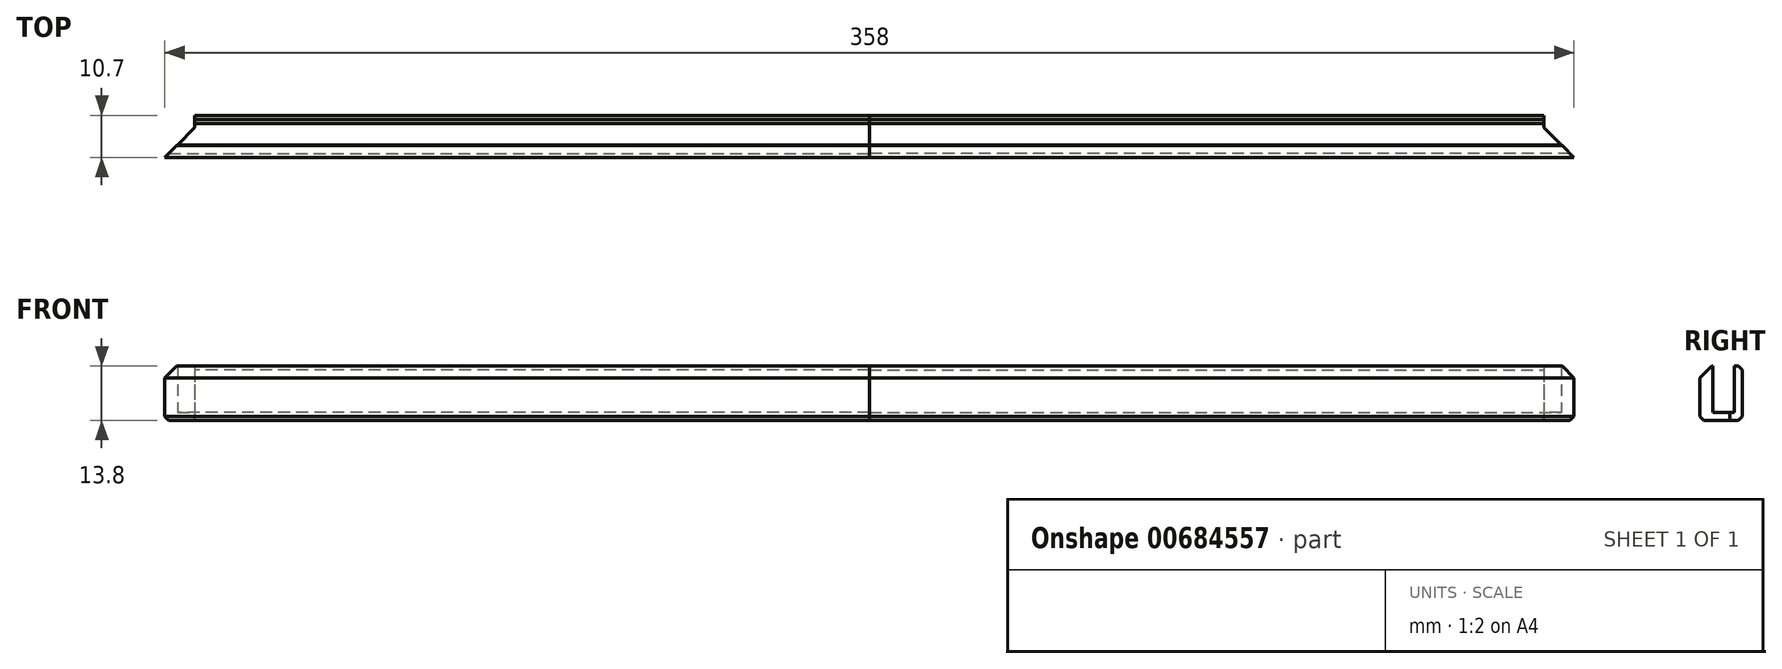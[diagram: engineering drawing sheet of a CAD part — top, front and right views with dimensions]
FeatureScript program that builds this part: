
annotation { "Feature Type Name" : "Feature", "Feature Type Description" : "" }
export const myFeature = defineFeature(function(context is Context, id is Id, definition is map)
    precondition{}
    {
        {
            var Q0;
            Q0=qCreatedBy(makeId("Top.planeOp"),FACE);
            var sketch = newSketch(context, id + "F0", { "sketchPlane" : qUnion([Q0])});
            skLineSegment(sketch, "E0.bottom", {"start": v(0, 0) * mm, "end": v(179, 0) * mm});
            skLineSegment(sketch, "E0.top", {"start": v(0, 10.7) * mm, "end": v(171.4, 10.7) * mm});
            skLineSegment(sketch, "E0.left", {"start": v(0, 0) * mm, "end": v(0, 10.7) * mm});
            skLineSegment(sketch, "E1", {"start": v(179, 0) * mm, "end": v(171.4, 7.6) * mm});
            skLineSegment(sketch, "E2", {"start": v(171.4, 7.6) * mm, "end": v(171.4, 10.7) * mm});
            skSolve(sketch);
        }
        {
            var Q0;
            Q0=makeQuery(id+"F0.imprint","IMPRINT",FACE,{"disambiguationData":[TD([[makeQuery(id+"F0.imprint","IMPRINT",EDGE,{"derivedFrom":sQuery(id+"F0.wireOp",EDGE,"E0.bottom")}),1.0]])]});
            extrude(context, id + "F1", {"entities" : qUnion([Q0]), "depth" : 2 * mm, "offsetDistance" : 25 * mm});
        }
        {
            var Q0;
            Q0=makeQuery(id+"F1.opExtrude","CAP_FACE",FACE,{"disambiguationData":[OSD([sQuery(id+"F0.wireOp",EDGE,"E0.bottom"),sQuery(id+"F0.wireOp",EDGE,"E0.top"),sQuery(id+"F0.wireOp",EDGE,"E0.left"),sQuery(id+"F0.wireOp",EDGE,"E1"),sQuery(id+"F0.wireOp",EDGE,"E2")])],"isStart":false});
            var sketch = newSketch(context, id + "F2", { "sketchPlane" : qUnion([Q0])});
            skLineSegment(sketch, "E3.bottom", {"start": v(0, 8.7) * mm, "end": v(179, 8.7) * mm});
            skLineSegment(sketch, "E3.top", {"start": v(0, 3.2) * mm, "end": v(179, 3.2) * mm});
            skLineSegment(sketch, "E3.left", {"start": v(0, 8.7) * mm, "end": v(0, 3.2) * mm});
            skLineSegment(sketch, "E3.right", {"start": v(179, 8.7) * mm, "end": v(179, 3.2) * mm});
            skSolve(sketch);
        }
        {
            var Q0;
            {var subQ5=makeQuery(id+"F1.opExtrude","CAP_EDGE",EDGE,{"disambiguationData":[OSD([sQuery(id+"F0.wireOp",EDGE,"E0.bottom")])],"isStart":false});Q0=makeQuery(id+"F2.imprint","IMPRINT",FACE,{"disambiguationData":[TD([[makeQuery(id+"F2.imprint","IMPRINT",EDGE,{"derivedFrom":subQ5}),1.0]])]});}
            var Q1;
            {var subQ4=makeQuery(id+"F1.opExtrude","CAP_EDGE",EDGE,{"disambiguationData":[OSD([sQuery(id+"F0.wireOp",EDGE,"E0.top")])],"isStart":false});Q1=makeQuery(id+"F2.imprint","IMPRINT",FACE,{"disambiguationData":[TD([[makeQuery(id+"F2.imprint","IMPRINT",EDGE,{"derivedFrom":subQ4}),-1.0]])]});}
            extrude(context, id + "F3", {"entities" : qUnion([Q0, Q1]), "operationType" : NewBodyOperationType.ADD, "depth" : 11.8 * mm, "offsetDistance" : 25 * mm});
        }
        {
            var Q0;
            Q0=makeQuery(id+"F3.opExtrude","CAP_EDGE",EDGE,{"disambiguationData":[OSD([sQuery(id+"F0.wireOp",EDGE,"E0.bottom")])],"isStart":false});
            chamfer(context, id + "F4", {"entities" : qUnion([Q0]), "width" : 3 * mm, "tangentPropagation" : true});
        }
        {
            var Q0;
            Q0=makeQuery(id+"F1.opExtrude","CAP_EDGE",EDGE,{"disambiguationData":[OSD([sQuery(id+"F0.wireOp",EDGE,"E0.bottom")])],"isStart":true});
            var Q1;
            Q1=makeQuery(id+"F1.opExtrude","CAP_EDGE",EDGE,{"disambiguationData":[OSD([sQuery(id+"F0.wireOp",EDGE,"E0.top")])],"isStart":true});
            var Q2;
            Q2=makeQuery(id+"F3.opExtrude","CAP_EDGE",EDGE,{"disambiguationData":[OSD([sQuery(id+"F0.wireOp",EDGE,"E0.top")])],"isStart":false});
            chamfer(context, id + "F5", {"entities" : qUnion([Q0, Q1, Q2]), "width" : 1 * mm, "tangentPropagation" : true});
        }
        {
            var Q0;
            Q0=makeQuery(id+"F1.opExtrude","SWEPT_BODY",BODY,{"disambiguationData":[OSD([sQuery(id+"F0.wireOp",EDGE,"E0.bottom"),sQuery(id+"F0.wireOp",EDGE,"E0.top"),sQuery(id+"F0.wireOp",EDGE,"E0.left"),sQuery(id+"F0.wireOp",EDGE,"E1"),sQuery(id+"F0.wireOp",EDGE,"E2")])]});
            var Q1;
            Q1=qCreatedBy(makeId("Right.planeOp"),FACE);
            mirror(context, id + "F6", {"entities" : qUnion([Q0]), "mirrorPlane" : qUnion([Q1])});
        }
    });
